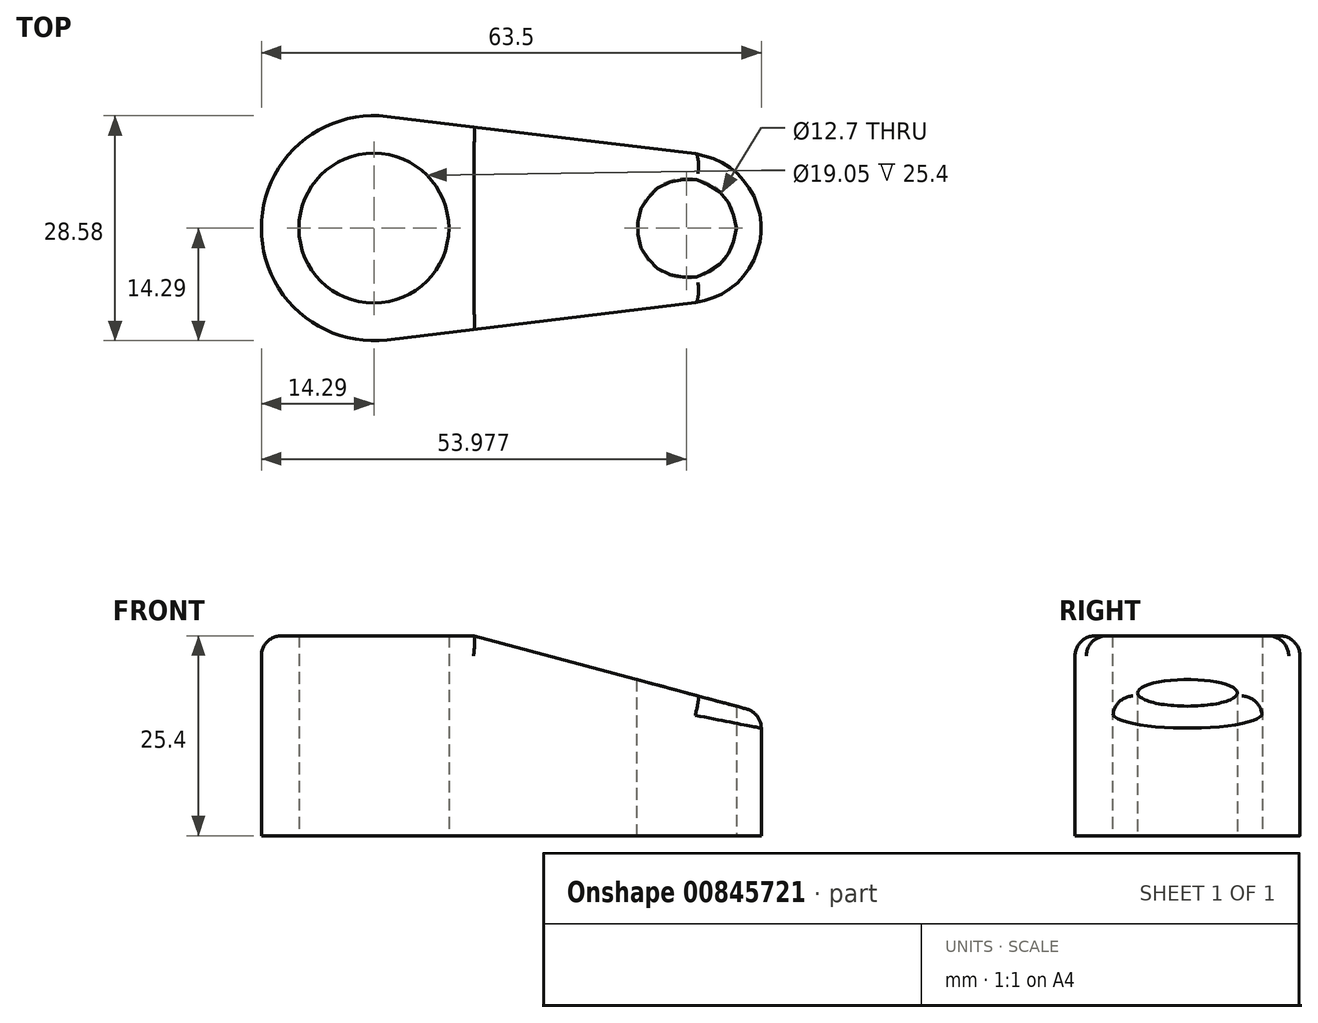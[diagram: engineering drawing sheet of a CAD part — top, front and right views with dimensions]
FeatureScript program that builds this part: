
annotation { "Feature Type Name" : "Feature", "Feature Type Description" : "" }
export const myFeature = defineFeature(function(context is Context, id is Id, definition is map)
    precondition{}
    {
        {
            var Q0;
            Q0=qCreatedBy(makeId("Top.planeOp"),FACE);
            var sketch = newSketch(context, id + "F0", { "sketchPlane" : qUnion([Q0])});
            skCircle(sketch, "E0", {"center": v(0, 0) * mm, "radius": 9.53 * mm});
            skCircle(sketch, "E1", {"center": v(39.69, 0) * mm, "radius": 6.35 * mm});
            skCircle(sketch, "E2", {"center": v(0, 0) * mm, "radius": 14.29 * mm});
            skCircle(sketch, "E3", {"center": v(39.69, 0) * mm, "radius": 9.53 * mm});
            skLineSegment(sketch, "E4", {"start": v(1.71, 14.18) * mm, "end": v(40.83, 9.46) * mm});
            skLineSegment(sketch, "E5", {"start": v(1.71, -14.18) * mm, "end": v(40.83, -9.46) * mm});
            skSolve(sketch);
        }
        {
            var Q0;
            Q0=makeQuery(id+"F0.imprint","IMPRINT",FACE,{"disambiguationData":[TD([[makeQuery(id+"F0.imprint","IMPRINT",EDGE,{"derivedFrom":sQuery(id+"F0.wireOp",EDGE,"E0")}),-1.0]])]});
            var Q1;
            {var subQ0=sQuery(id+"F0.wireOp",EDGE,"E4");Q1=makeQuery(id+"F0.imprint","IMPRINT",FACE,{"disambiguationData":[TD([[makeQuery(id+"F0.imprint","IMPRINT",EDGE,{"derivedFrom":subQ0}),-1.0]])]});}
            var Q2;
            Q2=makeQuery(id+"F0.imprint","IMPRINT",FACE,{"disambiguationData":[TD([[makeQuery(id+"F0.imprint","IMPRINT",EDGE,{"derivedFrom":sQuery(id+"F0.wireOp",EDGE,"E1")}),-1.0]])]});
            extrude(context, id + "F1", {"entities" : qUnion([Q0, Q1, Q2]), "depth" : 25.4 * mm, "offsetDistance" : 25.4 * mm});
        }
        {
            var Q0;
            Q0=qCreatedBy(makeId("Front.planeOp"),FACE);
            var sketch = newSketch(context, id + "F2", { "sketchPlane" : qUnion([Q0])});
            skLineSegment(sketch, "E6", {"start": v(12.7, 25.4) * mm, "end": v(49.21, 25.4) * mm});
            skLineSegment(sketch, "E7", {"start": v(49.21, 25.4) * mm, "end": v(49.21, 15.62) * mm});
            skLineSegment(sketch, "E8", {"start": v(49.21, 15.62) * mm, "end": v(12.7, 25.4) * mm});
            skLineSegment(sketch, "E9.0", {"start": v(40.83, 25.4) * mm, "end": v(40.83, 0) * mm});
            skLineSegment(sketch, "E10", {"start": v(49.21, 25.4) * mm, "end": v(49.21, 0) * mm});
            skSolve(sketch);
        }
        {
            var Q0;
            Q0 = qSketchRegion(id + "F2", true);
            extrude(context, id + "F3", {"entities" : qUnion([Q0]), "operationType" : NewBodyOperationType.REMOVE, "endBound" : BoundingType.SYMMETRIC, "oppositeDirection" : true, "depth" : 30.48 * mm, "offsetDistance" : 25.4 * mm});
        }
        {
            var Q0;
            Q0=makeQuery(id+"F3.boolean.opBoolean","INTERSECT",EDGE,{"derivedFrom":[makeQuery(id+"F1.opExtrude","SWEPT_FACE",FACE,{"disambiguationData":[OSD([sQuery(id+"F0.wireOp",EDGE,"E5")])]}),makeQuery(id+"F3.opExtrude","SWEPT_FACE",FACE,{"disambiguationData":[OSD([sQuery(id+"F2.wireOp",EDGE,"E8")])]})]});
            var Q1;
            Q1=makeQuery(id+"F1.opExtrude","CAP_EDGE",EDGE,{"disambiguationData":[OSD([sQuery(id+"F0.wireOp",EDGE,"E2")])],"isStart":false});
            fillet(context, id + "F4", {"entities" : qUnion([Q0, Q1]), "radius" : 2.54 * mm, "tangentPropagation" : true, "allowEdgeOverflow" : false});
        }
    });
